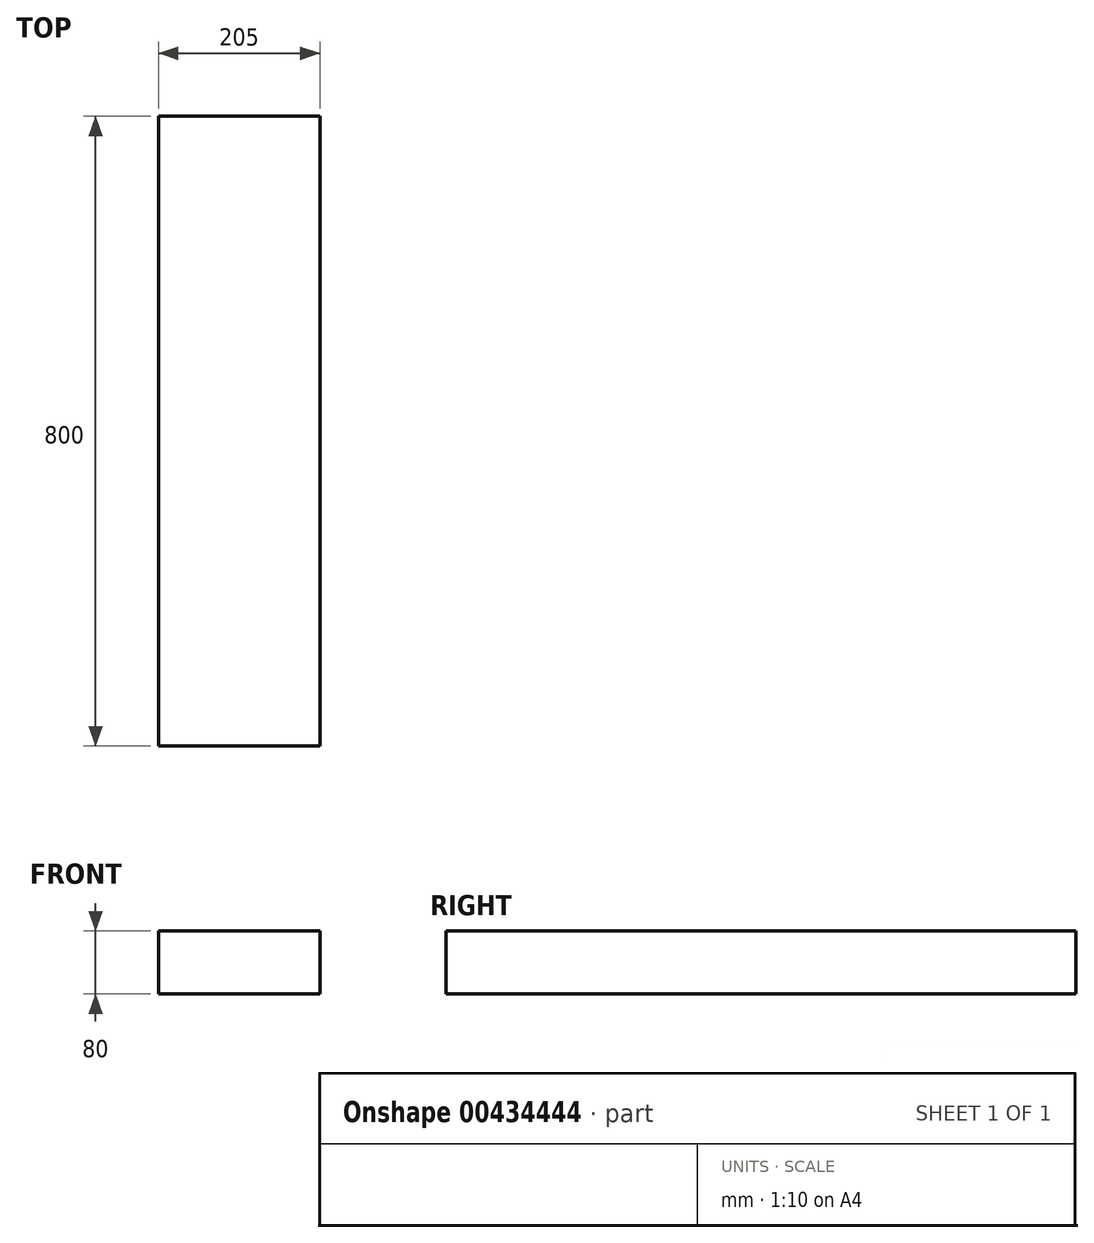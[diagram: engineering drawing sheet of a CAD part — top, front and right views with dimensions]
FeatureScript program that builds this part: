
annotation { "Feature Type Name" : "Feature", "Feature Type Description" : "" }
export const myFeature = defineFeature(function(context is Context, id is Id, definition is map)
    precondition{}
    {
        {
            var Q0;
            Q0=qCreatedBy(makeId("Front.planeOp"),FACE);
            var sketch = newSketch(context, id + "F0", { "sketchPlane" : qUnion([Q0])});
            skLineSegment(sketch, "E0.bottom", {"start": v(102.5, -40) * mm, "end": v(-102.5, -40) * mm});
            skLineSegment(sketch, "E0.top", {"start": v(102.5, 40) * mm, "end": v(-102.5, 40) * mm});
            skLineSegment(sketch, "E0.left", {"start": v(102.5, -40) * mm, "end": v(102.5, 40) * mm});
            skLineSegment(sketch, "E0.right", {"start": v(-102.5, -40) * mm, "end": v(-102.5, 40) * mm});
            skPoint(sketch, "E0.middle", {"position": v(0, 0) * mm});
            skSolve(sketch);
        }
        {
            var Q0;
            Q0 = qSketchRegion(id + "F0", true);
            extrude(context, id + "F1", {"entities" : qUnion([Q0]), "depth" : 800 * mm, "offsetDistance" : 25 * mm});
        }
    });
